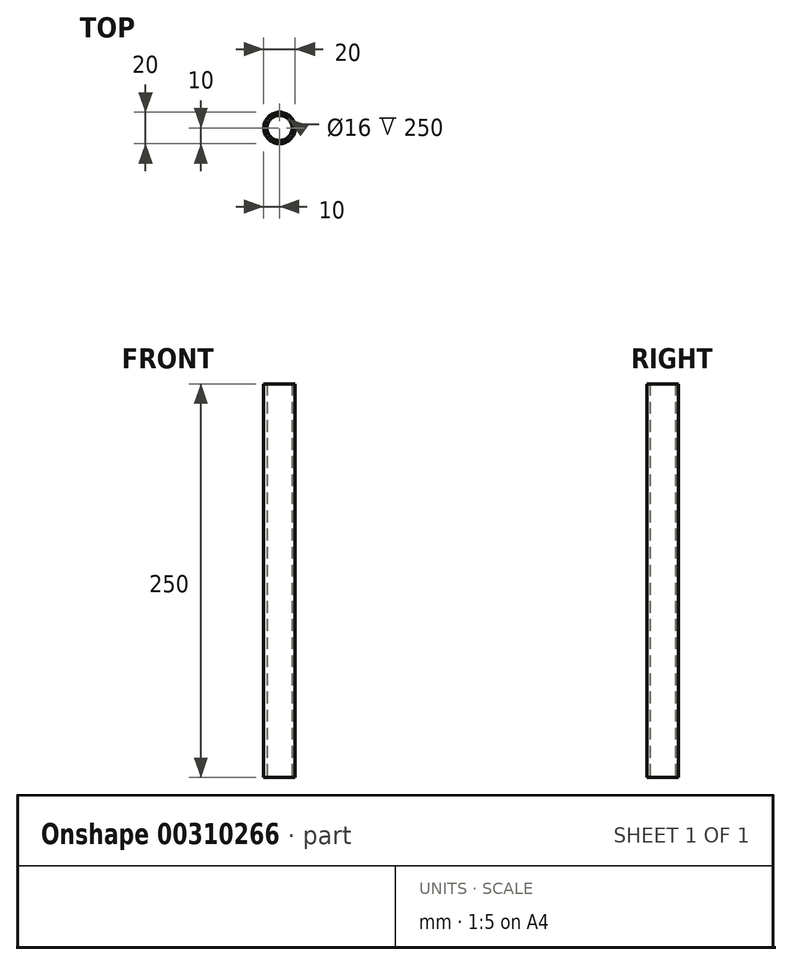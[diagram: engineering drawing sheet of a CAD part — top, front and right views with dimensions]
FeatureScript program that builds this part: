
annotation { "Feature Type Name" : "Feature", "Feature Type Description" : "" }
export const myFeature = defineFeature(function(context is Context, id is Id, definition is map)
    precondition{}
    {
        {
            var Q0;
            Q0=qCreatedBy(makeId("Top.planeOp"),FACE);
            var sketch = newSketch(context, id + "F0", { "sketchPlane" : qUnion([Q0])});
            skCircle(sketch, "E0", {"center": v(0, 0) * mm, "radius": 10 * mm});
            skCircle(sketch, "E1", {"center": v(0, 0) * mm, "radius": 8 * mm});
            skSolve(sketch);
        }
        {
            var Q0;
            Q0=qSketchRegion(id+"F0",true);
            extrude(context, id + "F1", {"entities" : qUnion([Q0]), "endBound" : BoundingType.SYMMETRIC, "depth" : 250 * mm});
        }
    });
